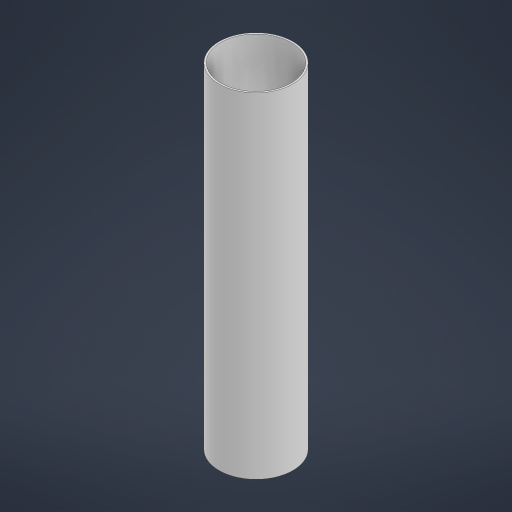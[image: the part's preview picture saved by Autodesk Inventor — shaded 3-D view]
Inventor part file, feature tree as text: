
AUTODESK INVENTOR PART (.ipt)
format: ipt  version: 2023 (Build 270158000, 158)  size: 164,352 bytes
history: native  units: mm
features: extrude x1, sketch x1
ambient origin geometry x8: Origin, YZ Plane, XZ Plane, XY Plane, X Axis, Y Axis, Z Axis, Center Point
bodies: Solid1 (feature_tree)
feature tree (2):
  extrude  "Extrusion1"  Depth=100.0mm
  sketch  "Sketch1"  dims[d0=21.0mm d1=22.0mm d2=100.0mm d3=0.0mm]
